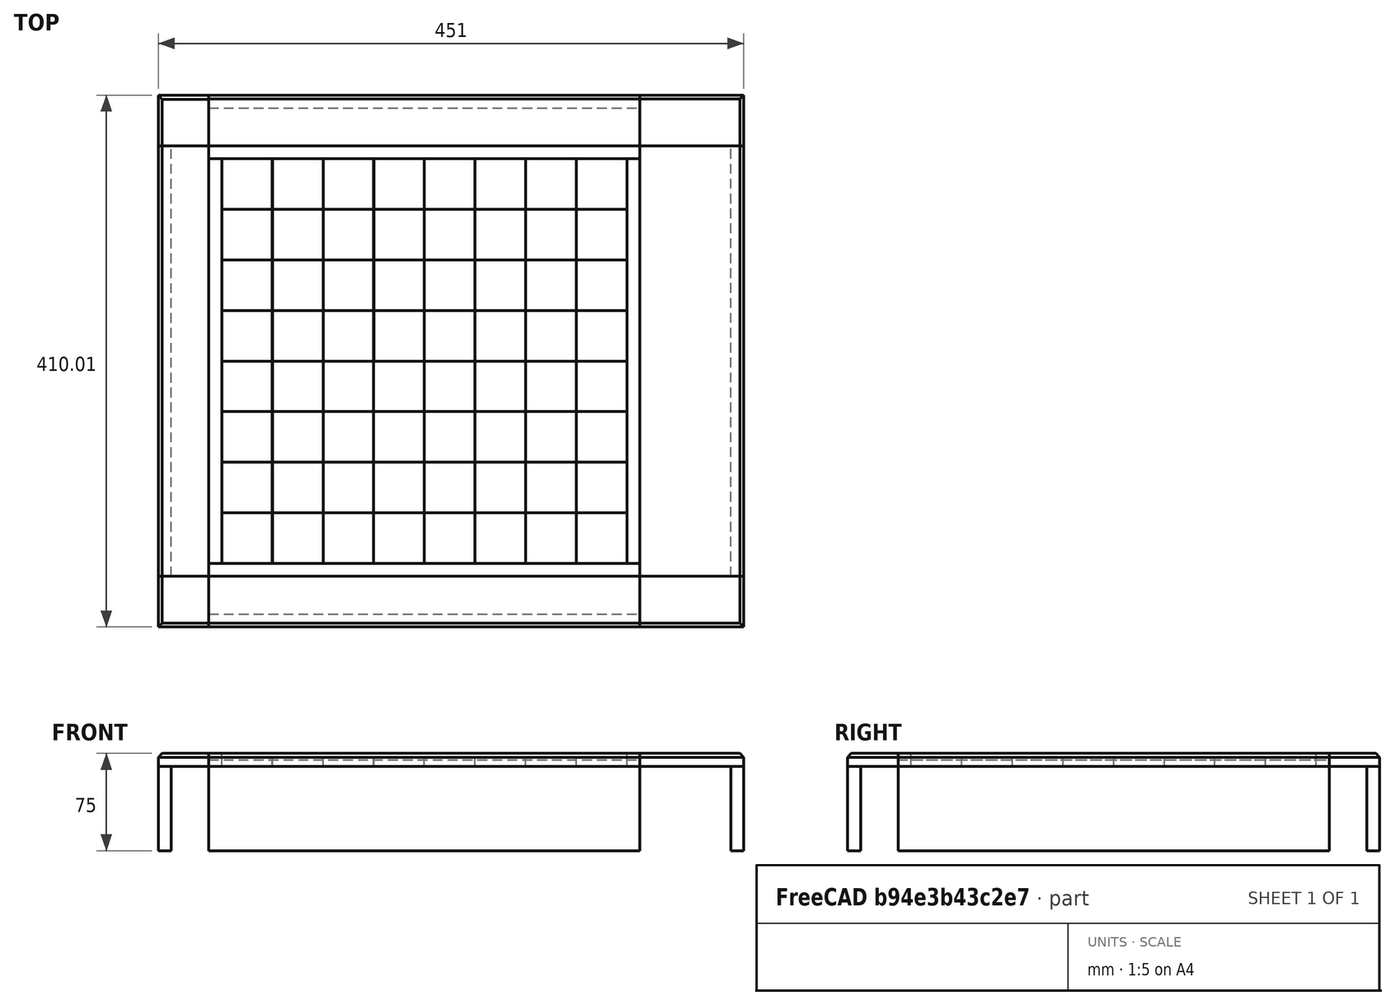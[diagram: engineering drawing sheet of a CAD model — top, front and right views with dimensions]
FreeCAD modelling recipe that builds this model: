
FCSTD DOCUMENT
Label: seb
objects: Part::Box×81, Part::Chamfer×8, App::DocumentObjectGroup×4
note: 89 computed .brp shape members not serialized (recipe doc carries the construction recipe); baked Part::Feature solids carry a one-line shape summary decoded from their .brp

FEATURE [Part::Box] Box002  label="Leiste1"
  Height = 5
  Length = 10
  Placement = pos=(-10,2.5e-10,5) rot=(0,0,1;0rad)
  Width = 312
FEATURE [Part::Box] Box002001  label="Leiste2"
  Height = 5
  Length = 10
  Placement = pos=(312,2.5e-10,5) rot=(0,0,1;0rad)
  Width = 312
FEATURE [Part::Box] Box002002  label="Leiste3"
  Height = 5
  Length = 332
  Placement = pos=(-9.99999,312,5) rot=(0,0,1;0rad)
  Width = 10
FEATURE [Part::Box] Box002002001  label="Leiste4"
  Height = 5
  Length = 332
  Placement = pos=(-10,-10,5) rot=(0,0,1;0rad)
  Width = 10
FEATURE [Part::Box] Box002002002  label="Kachelnboden"
  Height = 5
  Length = 332
  Placement = pos=(-10,-10,0) rot=(0,0,1;0rad)
  Width = 332
FEATURE [App::DocumentObjectGroup] Gruppe  label="Schachbrett"
  Group = -> [Box002,Box002001,Box002002,Box002002001,Box002002002]
FEATURE [Part::Box] Box  label="Kachel1"
  Height = 10
  Length = 39
  Placement = pos=(273.094,195,0) rot=(0,0,1;0rad)
  Width = 39
FEATURE [Part::Box] Box002002004  label="Kachel2"
  Height = 10
  Length = 39
  Placement = pos=(155.956,273,0) rot=(0,0,1;0rad)
  Width = 39
FEATURE [Part::Box] Box002002005  label="Kachel3"
  Height = 10
  Length = 39
  Placement = pos=(234.055,273,0) rot=(0,0,1;0rad)
  Width = 39
FEATURE [Part::Box] Box002002004001  label="Kachel4"
  Height = 10
  Length = 39
  Placement = pos=(195.055,273,0) rot=(0,0,1;0rad)
  Width = 39
FEATURE [Part::Box] Box002002004001001  label="Kachel5"
  Height = 10
  Length = 39
  Placement = pos=(195.055,234,0) rot=(0,0,1;0rad)
  Width = 39
FEATURE [Part::Box] Box002002005001  label="kachel6"
  Height = 10
  Length = 39
  Placement = pos=(234.055,234,0) rot=(0,0,1;0rad)
  Width = 39
FEATURE [Part::Box] Box002002004001002  label="Kachel7"
  Height = 10
  Length = 39
  Placement = pos=(155.956,234,0) rot=(0,0,1;0rad)
  Width = 39
FEATURE [Part::Box] Box002002004001003  label="kachel8"
  Height = 10
  Length = 39
  Placement = pos=(273.094,234,0) rot=(0,0,1;0rad)
  Width = 39
FEATURE [Part::Box] Box002002004001005  label="Kachel9"
  Height = 10
  Length = 39
  Placement = pos=(273.094,273,0) rot=(0,0,1;0rad)
  Width = 39
FEATURE [Part::Box] Box002002004001006  label="Kachel10"
  Height = 10
  Length = 39
  Placement = pos=(155.956,195,0) rot=(0,0,1;0rad)
  Width = 39
FEATURE [Part::Box] Box002002005002  label="Kachel11"
  Height = 10
  Length = 39
  Placement = pos=(234.055,195,0) rot=(0,0,1;0rad)
  Width = 39
FEATURE [Part::Box] Box002002004001007  label="Kachel12"
  Height = 10
  Length = 39
  Placement = pos=(195.055,195,0) rot=(0,0,1;0rad)
  Width = 39
FEATURE [Part::Box] Box002002004001001001  label="Kachel13"
  Height = 10
  Length = 39
  Placement = pos=(195.055,156,0) rot=(0,0,1;0rad)
  Width = 39
FEATURE [Part::Box] Box002002005001001  label="Kachel14"
  Height = 10
  Length = 39
  Placement = pos=(234.055,156,0) rot=(0,0,1;0rad)
  Width = 39
FEATURE [Part::Box] Box002002004001002001  label="kachel15"
  Height = 10
  Length = 39
  Placement = pos=(155.956,156,0) rot=(0,0,1;0rad)
  Width = 39
FEATURE [Part::Box] Box002002004001003001  label="Kachel16"
  Height = 10
  Length = 39
  Placement = pos=(273.094,156,0) rot=(0,0,1;0rad)
  Width = 39
FEATURE [Part::Box] Box002002004001003001001  label="Kachel17"
  Height = 10
  Length = 39
  Placement = pos=(117.055,156,0) rot=(0,0,1;0rad)
  Width = 39
FEATURE [Part::Box] Box002002004001002001001
  Height = 10
  Length = 39
  Placement = pos=(-0.083067,156,0) rot=(0,0,1;0rad)
  Width = 39
FEATURE [Part::Box] Box002002005001001001
  Height = 10
  Length = 39
  Placement = pos=(78.0165,156,0) rot=(0,0,1;0rad)
  Width = 39
FEATURE [Part::Box] Box002002004001001001001
  Height = 10
  Length = 39
  Placement = pos=(39.0165,156,0) rot=(0,0,1;0rad)
  Width = 39
FEATURE [Part::Box] Box002002004001007001
  Height = 10
  Length = 39
  Placement = pos=(39.0165,195,0) rot=(0,0,1;0rad)
  Width = 39
FEATURE [Part::Box] Box002002005002001
  Height = 10
  Length = 39
  Placement = pos=(78.0165,195,0) rot=(0,0,1;0rad)
  Width = 39
FEATURE [Part::Box] Box002002004001006001
  Height = 10
  Length = 39
  Placement = pos=(-0.083067,195,0) rot=(0,0,1;0rad)
  Width = 39
FEATURE [Part::Box] Box002002004001005001
  Height = 10
  Length = 39
  Placement = pos=(117.055,273,0) rot=(0,0,1;0rad)
  Width = 39
FEATURE [Part::Box] Box002002004001003001002
  Height = 10
  Length = 39
  Placement = pos=(117.055,234,0) rot=(0,0,1;0rad)
  Width = 39
FEATURE [Part::Box] Box002002004001002001002
  Height = 10
  Length = 39
  Placement = pos=(-0.083067,234,0) rot=(0,0,1;0rad)
  Width = 39
FEATURE [Part::Box] Box002002004001001001002
  Height = 10
  Length = 39
  Placement = pos=(39.0165,234,0) rot=(0,0,1;0rad)
  Width = 39
FEATURE [Part::Box] Box002002005001001002
  Height = 10
  Length = 39
  Placement = pos=(78.0165,234,0) rot=(0,0,1;0rad)
  Width = 39
FEATURE [Part::Box] Box002002005001001003
  Height = 10
  Length = 39
  Placement = pos=(78.0165,273,0) rot=(0,0,1;0rad)
  Width = 39
FEATURE [Part::Box] Box002002004001003001003
  Height = 10
  Length = 39
  Placement = pos=(-0.083067,273,0) rot=(0,0,1;0rad)
  Width = 39
FEATURE [Part::Box] Box002002004001003001004
  Height = 10
  Length = 39
  Placement = pos=(39.0165,273,0) rot=(0,0,1;0rad)
  Width = 39
FEATURE [Part::Box] Box002002004001003001005
  Height = 10
  Length = 39
  Placement = pos=(117.055,195,0) rot=(0,0,1;0rad)
  Width = 39
FEATURE [Part::Box] Box002002004001003001006
  Height = 10
  Length = 39
  Placement = pos=(273.077,39,0) rot=(0,0,1;0rad)
  Width = 39
FEATURE [Part::Box] Box002002004001003001001001
  Height = 10
  Length = 39
  Placement = pos=(117.039,0,0) rot=(0,0,1;0rad)
  Width = 39
FEATURE [Part::Box] Box002002005001001004
  Height = 10
  Length = 39
  Placement = pos=(234.039,117,0) rot=(0,0,1;0rad)
  Width = 39
FEATURE [Part::Box] Box002002004001002001001001
  Height = 10
  Length = 39
  Placement = pos=(-0.0996106,2.5e-10,0) rot=(0,0,1;0rad)
  Width = 39
FEATURE [Part::Box] Box002002005001001001001
  Height = 10
  Length = 39
  Placement = pos=(78,-3.8147e-06,0) rot=(0,0,1;0rad)
  Width = 39
FEATURE [Part::Box] Box002002004001001001001001
  Height = 10
  Length = 39
  Placement = pos=(39,0,0) rot=(0,0,1;0rad)
  Width = 39
FEATURE [Part::Box] Box002002004001007001001
  Height = 10
  Length = 39
  Placement = pos=(39,39,0) rot=(0,0,1;0rad)
  Width = 39
FEATURE [Part::Box] Box002002005002001001
  Height = 10
  Length = 39
  Placement = pos=(78,39,0) rot=(0,0,1;0rad)
  Width = 39
FEATURE [Part::Box] Box002002004001006001001
  Height = 10
  Length = 39
  Placement = pos=(-0.0996106,39,0) rot=(0,0,1;0rad)
  Width = 39
FEATURE [Part::Box] Box002002004001005001001
  Height = 10
  Length = 39
  Placement = pos=(117.039,117,0) rot=(0,0,1;0rad)
  Width = 39
FEATURE [Part::Box] Box002002004001001001002001
  Height = 10
  Length = 39
  Placement = pos=(39,78,0) rot=(0,0,1;0rad)
  Width = 39
FEATURE [Part::Box] Box002002004001003001002001
  Height = 10
  Length = 39
  Placement = pos=(117.039,78,0) rot=(0,0,1;0rad)
  Width = 39
FEATURE [Part::Box] Box002002005001001002001
  Height = 10
  Length = 39
  Placement = pos=(78,78,0) rot=(0,0,1;0rad)
  Width = 39
FEATURE [Part::Box] Box002002005001001003001
  Height = 10
  Length = 39
  Placement = pos=(78,117,0) rot=(0,0,1;0rad)
  Width = 39
FEATURE [Part::Box] Box002002004001002001002001
  Height = 10
  Length = 39
  Placement = pos=(-0.0996106,78,0) rot=(0,0,1;0rad)
  Width = 39
FEATURE [Part::Box] Box002002004001003001003001
  Height = 10
  Length = 39
  Placement = pos=(-0.0996106,117,0) rot=(0,0,1;0rad)
  Width = 39
FEATURE [Part::Box] Box002002004001003001004001
  Height = 10
  Length = 39
  Placement = pos=(39,117,0) rot=(0,0,1;0rad)
  Width = 39
FEATURE [Part::Box] Box002002004001003001005001
  Height = 10
  Length = 39
  Placement = pos=(117.039,39,0) rot=(0,0,1;0rad)
  Width = 39
FEATURE [Part::Box] Box002002005001001003002
  Height = 10
  Length = 39
  Placement = pos=(234.039,-3.81495e-06,0) rot=(0,0,1;0rad)
  Width = 39
FEATURE [Part::Box] Box002002004001002001002002
  Height = 10
  Length = 39
  Placement = pos=(155.939,0,0) rot=(0,0,1;0rad)
  Width = 39
FEATURE [Part::Box] Box002002004001003001005002
  Height = 10
  Length = 39
  Placement = pos=(273.077,-2.5e-10,0) rot=(0,0,1;0rad)
  Width = 39
FEATURE [Part::Box] Box002002004001003001005003
  Height = 10
  Length = 39
  Placement = pos=(155.939,117,0) rot=(0,0,1;0rad)
  Width = 39
FEATURE [Part::Box] Box002002004001001001002002
  Height = 10
  Length = 39
  Placement = pos=(195.039,78,0) rot=(0,0,1;0rad)
  Width = 39
FEATURE [Part::Box] Box002002004001003001005004
  Height = 10
  Length = 39
  Placement = pos=(195.039,117,0) rot=(0,0,1;0rad)
  Width = 39
FEATURE [Part::Box] Box002002004001001001002003
  Height = 10
  Length = 39
  Placement = pos=(195.039,-2.5e-10,0) rot=(0,0,1;0rad)
  Width = 39
FEATURE [Part::Box] Box002002004001007001002
  Height = 10
  Length = 39
  Placement = pos=(195.039,39,0) rot=(0,0,1;0rad)
  Width = 39
FEATURE [Part::Box] Box002002005001001003003
  Height = 10
  Length = 39
  Placement = pos=(234.039,78,0) rot=(0,0,1;0rad)
  Width = 39
FEATURE [Part::Box] Box002002005002001002
  Height = 10
  Length = 39
  Placement = pos=(234.039,39,0) rot=(0,0,1;0rad)
  Width = 39
FEATURE [Part::Box] Box002002004001006001002
  Height = 10
  Length = 39
  Placement = pos=(155.939,39,0) rot=(0,0,1;0rad)
  Width = 39
FEATURE [Part::Box] Box002002004001005001002
  Height = 10
  Length = 39
  Placement = pos=(273.077,117,0) rot=(0,0,1;0rad)
  Width = 39
FEATURE [Part::Box] Box002002004001003001005005
  Height = 10
  Length = 39
  Placement = pos=(273.077,78,0) rot=(0,0,1;0rad)
  Width = 39
FEATURE [Part::Box] Box002002004001002001002003
  Height = 10
  Length = 39
  Placement = pos=(155.939,78,0) rot=(0,0,1;0rad)
  Width = 39
FEATURE [App::DocumentObjectGroup] Gruppe003  label="Kacheln"
  Group = -> [Box,Box002002004,Box002002005,Box002002004001,Box002002004001001,Box002002005001,Box002002004001002,Box002002004001003,Box002002004001005,Box002002004001006,Box002002005002,Box002002004001007,Box002002004001001001,Box002002005001001,Box002002004001002001,Box002002004001003001,Box002002004001003001001,Box002002004001002001001,Box002002005001001001,Box002002004001001001001,Box002002004001007001,+43 more]
FEATURE [Part::Box] Box002002004001003001005006  label="Fuß1"
  Height = 10
  Length = 39
  Placement = pos=(-49,322,-65) rot=(0,0,1;0rad)
  Width = 39
FEATURE [Part::Box] Box002002004001003001005006001  label="Fuß2"
  Height = 10
  Length = 39
  Placement = pos=(-49,-49,-65) rot=(0,0,1;0rad)
  Width = 39
FEATURE [Part::Box] Box002002004001003001005006002  label="Fuß3"
  Height = 10
  Length = 80
  Placement = pos=(322,-48.9098,-65) rot=(0,0,1;0rad)
  Width = 39
FEATURE [Part::Box] Box002002004001003001005006003  label="Fuß4"
  Height = 10
  Length = 80
  Placement = pos=(322,321.995,-65) rot=(0,0,1;0rad)
  Width = 39
FEATURE [Part::Box] Box002002004001003001005006004  label="Rand1"
  Height = 10
  Length = 332
  Placement = pos=(-10.0002,321.995,-4.52349e-07) rot=(0,0,1;0rad)
  Width = 39
FEATURE [Part::Box] Box002002004001003001005006004001  label="Rand2"
  Height = 10
  Length = 39
  Placement = pos=(-49,-10,0) rot=(0,0,1;0rad)
  Width = 332
FEATURE [Part::Box] Box002002004001003001005006004002  label="Rand3"
  Height = 10
  Length = 80
  Placement = pos=(322,-10,0) rot=(0,0,1;0rad)
  Width = 332
FEATURE [Part::Box] Box002002004001003001005006004003  label="Rand4"
  Height = 10
  Length = 332
  Placement = pos=(-9.97543,-48.9207,1.455e-06) rot=(0,0,1;0rad)
  Width = 39
FEATURE [Part::Box] Box002002004001003001005006004004  label="Seiten Rand1"
  Height = 65
  Length = 332
  Placement = pos=(-9.97565,351.008,-65) rot=(0,0,1;0rad)
  Width = 10
FEATURE [Part::Box] Box002002004001003001005006004004001  label="Seiten Rand2"
  Height = 65
  Length = 332
  Placement = pos=(-9.97543,-48.9207,-65) rot=(0,0,1;0rad)
  Width = 10
FEATURE [Part::Box] Box002002004001003001005006004004002  label="Seiten Rand3"
  Height = 65
  Length = 10
  Placement = pos=(392,-9.90981,-65) rot=(0,0,1;0rad)
  Width = 332
FEATURE [Part::Box] Box002002004001003001005006004004002001  label="Seiten Rand4"
  Height = 65
  Length = 10
  Placement = pos=(-49,-9.99999,-65) rot=(0,0,1;0rad)
  Width = 332
FEATURE [Part::Chamfer] Chamfer
  Base = -> Box002002004001003001005006002
  Edges = 2 edges r=3: [Edge6,Edge10]
  Placement = pos=(2.2303e-05,-0.090195,65) rot=(0,0,1;0rad)
FEATURE [Part::Chamfer] Chamfer001
  Base = -> Box002002004001003001005006004
  Edges = 1 edges r=3: [Edge12]
FEATURE [Part::Chamfer] Chamfer002
  Base = -> Box002002004001003001005006004002
  Edges = 1 edges r=3: [Edge6]
FEATURE [Part::Chamfer] Chamfer003
  Base = -> Box002002004001003001005006004003
  Edges = 1 edges r=3: [Edge10]
  Placement = pos=(-0.0245495,-0.0793037,-1.90735e-06) rot=(0,0,1;0rad)
FEATURE [Part::Chamfer] Chamfer004
  Base = -> Box002002004001003001005006004001
  Edges = 1 edges r=3: [Edge2]
FEATURE [App::DocumentObjectGroup] Gruppe005  label="Ober und seiten Rand"
  Group = -> [Box002002004001003001005006004004002001,Box002002004001003001005006004004,Box002002004001003001005006004004002,Box002002004001003001005006004004001,Box002002004001003001005006004,Box002002004001003001005006004001,Box002002004001003001005006004002,Box002002004001003001005006004003,Chamfer001,Chamfer002,Chamfer003,Chamfer004]
FEATURE [Part::Chamfer] Chamfer005
  Base = -> Box002002004001003001005006001
  Edges = 2 edges r=3: [Edge2,Edge10]
  Placement = pos=(0.0245667,0.0793037,65) rot=(0,0,1;0rad)
FEATURE [Part::Chamfer] Chamfer006
  Base = -> Box002002004001003001005006
  Edges = 2 edges r=3: [Edge2,Edge12]
  Placement = pos=(1.9077e-06,-0.0901947,65) rot=(0,0,1;0rad)
FEATURE [Part::Chamfer] Chamfer007
  Base = -> Box002002004001003001005006003
  Edges = 2 edges r=3: [Edge6,Edge12]
  Placement = pos=(0.000215531,0.00543213,65) rot=(0,0,1;0rad)
FEATURE [App::DocumentObjectGroup] Gruppe004  label="Fuß"
  Group = -> [Box002002004001003001005006,Box002002004001003001005006001,Box002002004001003001005006002,Box002002004001003001005006003,Chamfer,Chamfer007,Chamfer005,Chamfer006]
